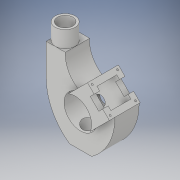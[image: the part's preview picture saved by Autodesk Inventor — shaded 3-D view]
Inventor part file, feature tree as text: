
AUTODESK INVENTOR PART (.ipt)
format: ipt  version: 2019 (Build 230136000, 136)  size: 332,800 bytes
history: native  units: mm
features: sketch x18, extrude x14, projected_geometry x3, sweep x2, other x2
ambient origin geometry x8: Origin, YZ Plane, XZ Plane, XY Plane, X Axis, Y Axis, Z Axis, Center Point
bodies: Body1 (feature_tree)
feature tree (39):
  extrude  "Extrusion2"  Depth=80.0mm
  sketch  "Esquisse3"
  sweep  "Balayage1"
  extrude  "Extrusion6"  Depth=30.0mm
  extrude  "Extrusion7"  Depth=18.0mm TaperAngle=0.0deg
  extrude  "Extrusion8"  TaperAngle=135.0deg  [1 undecoded]
  sketch  "Esquisse11"
  sketch  "Esquisse12"
  other  "Plan de construction1"
  sketch  "Esquisse13"
  extrude  "Extrusion9"  Depth=23.0mm
  extrude  "Extrusion10"  Depth=14.0mm
  other  "Plan de construction2"
  sketch  "Esquisse14"
  extrude  "Extrusion11"  Depth=4.0mm
  extrude  "Extrusion12"  TaperAngle=0.0deg  [1 undecoded]
  extrude  "Extrusion13"  Depth=4.0mm TaperAngle=0.0deg
  extrude  "Extrusion14"  Depth=9.0mm
  extrude  "Extrusion15"  Depth=4.0mm TaperAngle=0.0deg
  sketch  "Esquisse20"
  sketch  "Esquisse21"
  sketch  "Esquisse24"
  extrude  "Extrusion17"  Depth=2.0mm
  sweep  "Balayage4"
  extrude  "Extrusion18"  Depth=35.0mm
  extrude  "Extrusion19"  Depth=17.5mm
  sketch  "Esquisse2"
  sketch  "Esquisse4"
  sketch  "Esquisse8"
  sketch  "Esquisse9"
  sketch  "Esquisse10"
  sketch  "Esquisse16"
  projected_geometry  "Boucle projetée3"
  sketch  "Esquisse18"
  sketch  "Esquisse19"
  projected_geometry  "Boucle projetée4"
  projected_geometry  "Boucle projetée6"
  sketch  "Esquisse25"
  sketch  "Esquisse26"
note: 2 required parameter values undecoded (feature->parameter linkage not recoverable at this tier; creation-order binding heuristic only, values carry confidence <= 0.55)
